# Revit family: 304_Wafer-HF5-_
name_source: partatom
category: Pipe Accessories
units: mm (PartAtom-declared; Revit-internal decimal feet)

## family parameters
Always vertical = Yes
Cut with Voids When Loaded = No
Part Type = Valve - Breaks Into
Round Connector Dimension = Use Diameter
Shared = No
Work Plane-Based = No

## types (12) — shared parameters
CAT0 = Yes
Description = Wafer - Automatic Balancing Valve - Pre-Set Cartridge(s)
L2D_Min = 3048 mm
Manufacturer = FlowCon
QmdConnectorList = 301;D;302;D
URL = http://flowcon.com
magiPartTypeId = 304
magiProductFamilyId = Wafer-HF5-*
zero-valued in all types: MC_Default_elevation

## per-type parameters (varying)
| type | D | H1 | L | L1 | L2D | LL | R2 | W2D | magiProductId |
| F3345B-high flow | 150 mm | 200 mm  [stored 0.656168 ft] | 184 mm | 46 mm | 184 mm | 92 mm | 110 mm | 150 mm  [stored 0.492126 ft] | Wafer-HF5-150 |
| F3955B-high flow | 1000 mm | 660 mm | 438 mm | 109 mm | 437 mm | 219 mm  [stored 0.718504 ft] | 570 mm | 1000 mm | Wafer-HF5-1000 |
| F3705B-high flow | 900 mm | 605 mm | 432 mm | 108 mm | 431 mm | 216 mm | 515 mm | 900 mm | Wafer-HF5-900 |
| F3305B-high flow | 800 mm | 532 mm | 432 mm | 108 mm | 431 mm | 216 mm | 442 mm | 800 mm | Wafer-HF5-800 |
| F3865B-high flow | 600 mm | 447 mm | 279 mm | 70 mm | 279 mm | 140 mm | 357 mm  [stored 1.17126 ft] | 600 mm | Wafer-HF5-600 |
| F3385B-high flow | 500 mm | 394 mm | 279 mm | 70 mm | 279 mm | 140 mm | 304 mm | 500 mm | Wafer-HF5-500 |
| F3855B-high flow | 450 mm | 363 mm  [stored 1.19094 ft] | 241 mm | 60 mm | 241 mm | 121 mm | 273 mm  [stored 0.895669 ft] | 450 mm | Wafer-HF5-450 |
| F3845B-high flow | 400 mm | 346 mm | 241 mm | 60 mm | 241 mm | 121 mm | 256 mm | 400 mm  [stored 1.31234 ft] | Wafer-HF5-400 |
| F3395B-high flow | 350 mm | 314 mm  [stored 1.03018 ft] | 203 mm  [stored 0.66601 ft] | 51 mm | 203 mm  [stored 0.66601 ft] | 102 mm | 224 mm  [stored 0.734908 ft] | 350 mm  [stored 1.14829 ft] | Wafer-HF5-350 |
| F3695B-high flow | 300 mm | 293 mm  [stored 0.961286 ft] | 203 mm  [stored 0.66601 ft] | 51 mm | 203 mm  [stored 0.66601 ft] | 102 mm | 203 mm  [stored 0.66601 ft] | 300 mm  [stored 0.984252 ft] | Wafer-HF5-300 |
| F3685B-high flow | 250 mm | 261 mm | 203 mm  [stored 0.66601 ft] | 51 mm | 203 mm  [stored 0.66601 ft] | 102 mm | 171 mm | 250 mm  [stored 0.82021 ft] | Wafer-HF5-250 |
| F3375B-high flow | 200 mm | 228 mm  [stored 0.748031 ft] | 184 mm | 46 mm | 184 mm | 92 mm | 138 mm  [stored 0.452756 ft] | 200 mm  [stored 0.656168 ft] | Wafer-HF5-200 |

note: column(s) folded — value = type name in every type: magiProductCode

note: [stored X ft] marks values corroborated as IEEE doubles in the binary element streams (Revit-internal decimal feet)

## geometry (parser evidence)
native form markers: Sweep x2
no freeform markers — native parametric forms only
